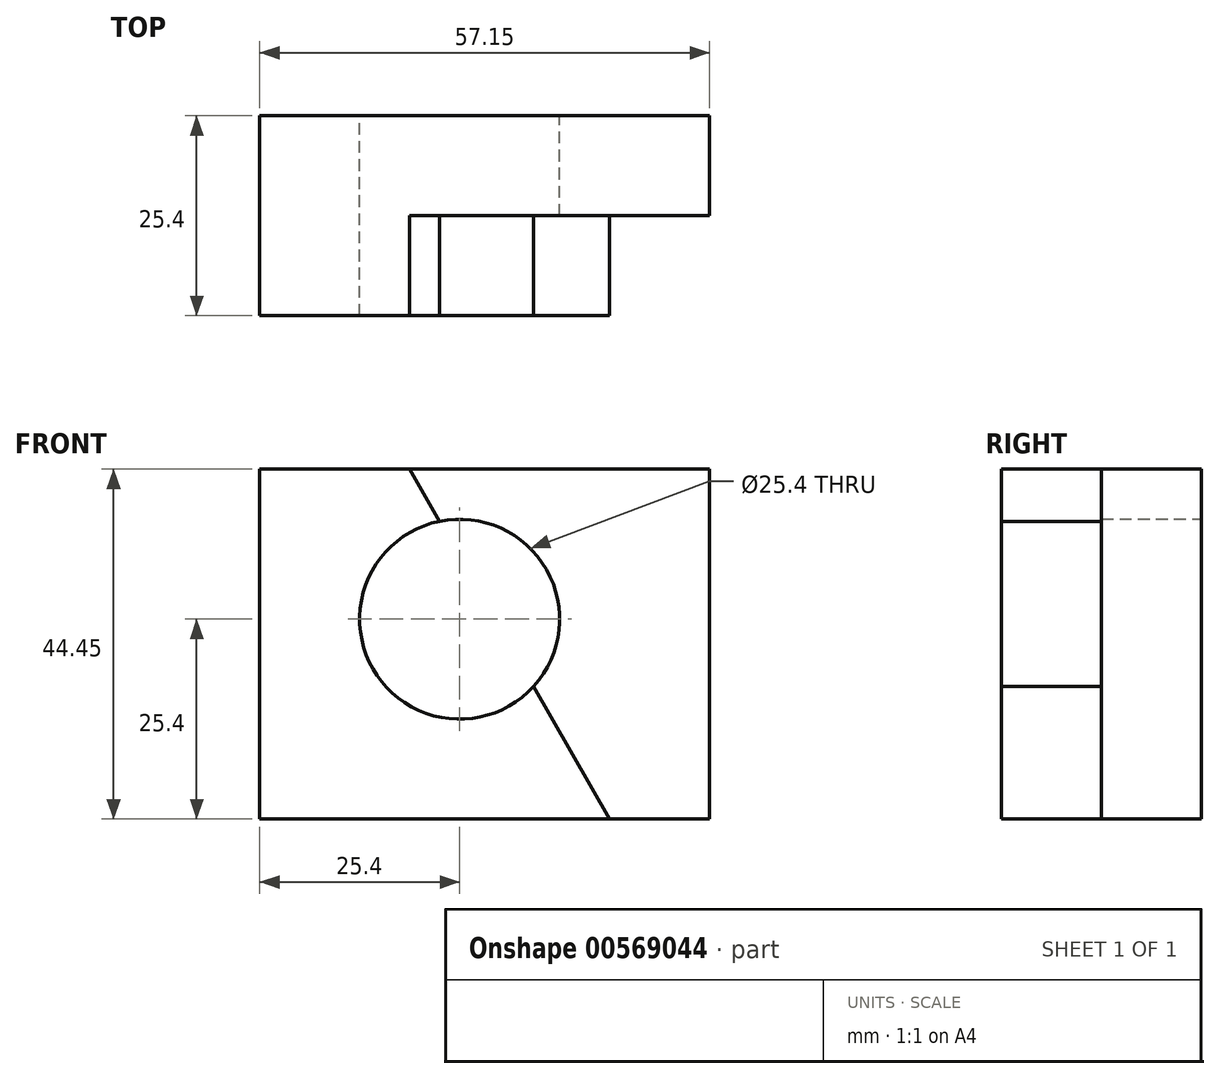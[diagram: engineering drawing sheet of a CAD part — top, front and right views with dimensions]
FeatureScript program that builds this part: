
annotation { "Feature Type Name" : "Feature", "Feature Type Description" : "" }
export const myFeature = defineFeature(function(context is Context, id is Id, definition is map)
    precondition{}
    {
        {
            var Q0;
            Q0=qCreatedBy(makeId("Front.planeOp"),FACE);
            var sketch = newSketch(context, id + "F0", { "sketchPlane" : qUnion([Q0])});
            skLineSegment(sketch, "E0", {"start": v(0, 0) * mm, "end": v(0, 44.45) * mm});
            skLineSegment(sketch, "E1", {"start": v(0, 44.45) * mm, "end": v(57.15, 44.45) * mm});
            skLineSegment(sketch, "E2", {"start": v(57.15, 44.45) * mm, "end": v(57.15, 0) * mm});
            skLineSegment(sketch, "E3", {"start": v(0, 0) * mm, "end": v(57.15, 0) * mm});
            skCircle(sketch, "E4", {"center": v(25.4, 25.4) * mm, "radius": 12.7 * mm});
            skSolve(sketch);
        }
        {
            var Q0;
            Q0=makeQuery(id+"F0.imprint","IMPRINT",FACE,{"disambiguationData":[TD([[makeQuery(id+"F0.imprint","IMPRINT",EDGE,{"derivedFrom":sQuery(id+"F0.wireOp",EDGE,"E0")}),-1.0]])]});
            extrude(context, id + "F1", {"entities" : qUnion([Q0]), "depth" : 25.4 * mm, "offsetDistance" : 25.4 * mm});
        }
        {
            var Q0;
            Q0=makeQuery(id+"F1.opExtrude","CAP_FACE",FACE,{"disambiguationData":[OSD([sQuery(id+"F0.wireOp",EDGE,"E0"),sQuery(id+"F0.wireOp",EDGE,"E1"),sQuery(id+"F0.wireOp",EDGE,"E2"),sQuery(id+"F0.wireOp",EDGE,"E3"),sQuery(id+"F0.wireOp",EDGE,"E4")])],"isStart":false});
            var sketch = newSketch(context, id + "F2", { "sketchPlane" : qUnion([Q0])});
            skLineSegment(sketch, "E5", {"start": v(19.05, 44.45) * mm, "end": v(44.45, 0) * mm});
            skSolve(sketch);
        }
        {
            var Q0;
            Q0 = qSketchRegion(id + "F2", true);
            var Q1;
            {var subQ0=makeQuery(id+"F1.opExtrude","CAP_EDGE",EDGE,{"disambiguationData":[OSD([sQuery(id+"F0.wireOp",EDGE,"E2")])],"isStart":false});Q1=makeQuery(id+"F2.imprint","IMPRINT",FACE,{"disambiguationData":[TD([[makeQuery(id+"F2.imprint","IMPRINT",EDGE,{"derivedFrom":subQ0}),-1.0]])]});}
            extrude(context, id + "F3", {"entities" : qUnion([Q0, Q1]), "operationType" : NewBodyOperationType.REMOVE, "oppositeDirection" : true, "depth" : 12.7 * mm, "offsetDistance" : 25.4 * mm});
        }
    });
